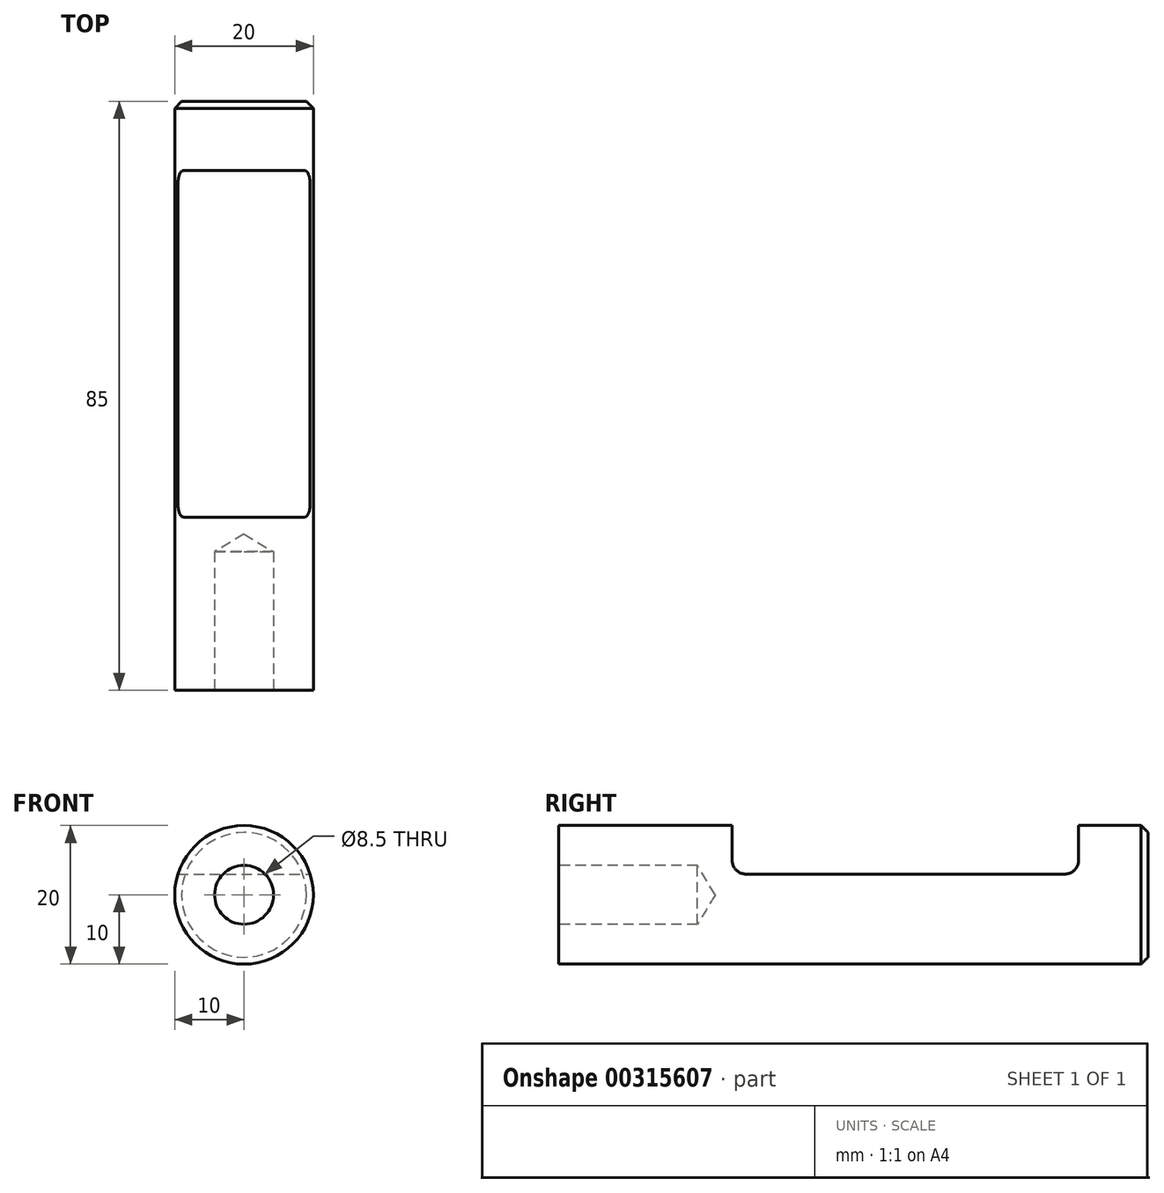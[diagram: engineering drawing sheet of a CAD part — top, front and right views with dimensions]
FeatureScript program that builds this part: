
annotation { "Feature Type Name" : "Feature", "Feature Type Description" : "" }
export const myFeature = defineFeature(function(context is Context, id is Id, definition is map)
    precondition{}
    {
        {
            var Q0;
            Q0=qCreatedBy(makeId("Front.planeOp"),FACE);
            var sketch = newSketch(context, id + "F0", { "sketchPlane" : qUnion([Q0])});
            skCircle(sketch, "E0", {"center": v(0, 0) * mm, "radius": 10 * mm});
            skSolve(sketch);
        }
        {
            var Q0;
            Q0 = qSketchRegion(id + "F0", true);
            extrude(context, id + "F1", {"entities" : qUnion([Q0]), "endBound" : BoundingType.SYMMETRIC, "depth" : 85 * mm});
        }
        {
            var Q0;
            Q0=makeQuery(id+"F1.opExtrude","CAP_FACE",FACE,{"disambiguationData":[OSD([sQuery(id+"F0.wireOp",EDGE,"E0")])],"isStart":false});
            var sketch = newSketch(context, id + "F2", { "sketchPlane" : qUnion([Q0])});
            skCircle(sketch, "E1", {"center": v(0, 0) * mm, "radius": 4.25 * mm});
            skSolve(sketch);
        }
        {
            var Q0;
            Q0=sQuery(id+"F2.wireOp",VERTEX,"E1.center");
            var Q1;
            Q1=makeQuery(id+"F1.opExtrude","SWEPT_BODY",BODY,{"disambiguationData":[OSD([sQuery(id+"F0.wireOp",EDGE,"E0")])]});
            hole(context, id + "F3", {"style" : HoleStyle.SIMPLE, "endStyle" : HoleEndStyle.BLIND, "holeDiameter" : 8.5 * mm, "holeDepth" : 20 * mm, "tappedDepth" : 12 * mm, "tapClearance" : 3, "locations" : qUnion([Q0]), "scope" : qUnion([Q1])});
        }
        {
            var Q0;
            Q0=makeQuery(id+"F1.opExtrude","CAP_EDGE",EDGE,{"disambiguationData":[OSD([sQuery(id+"F0.wireOp",EDGE,"E0")])],"isStart":true});
            chamfer(context, id + "F4", {"entities" : qUnion([Q0]), "width" : 1 * mm, "tangentPropagation" : true});
        }
        {
            var Q0;
            Q0=qCreatedBy(makeId("Right.planeOp"),FACE);
            var sketch = newSketch(context, id + "F5", { "sketchPlane" : qUnion([Q0])});
            skLineSegment(sketch, "E2.bottom", {"start": v(-17.5, 10) * mm, "end": v(32.5, 10) * mm});
            skLineSegment(sketch, "E2.top", {"start": v(-17.5, 3) * mm, "end": v(32.5, 3) * mm});
            skLineSegment(sketch, "E2.left", {"start": v(-17.5, 10) * mm, "end": v(-17.5, 3) * mm});
            skLineSegment(sketch, "E2.right", {"start": v(32.5, 10) * mm, "end": v(32.5, 3) * mm});
            skSolve(sketch);
        }
        {
            var Q0;
            Q0 = qSketchRegion(id + "F5", true);
            extrude(context, id + "F6", {"entities" : qUnion([Q0]), "operationType" : NewBodyOperationType.REMOVE, "endBound" : BoundingType.THROUGH_ALL, "oppositeDirection" : true, "depth" : 25 * mm, "hasSecondDirection" : true, "secondDirectionBound" : SecondDirectionBoundingType.THROUGH_ALL, "secondDirectionOppositeDirection" : false, "secondDirectionDepth" : 25 * mm});
        }
        {
            var Q0;
            Q0=makeQuery(id+"F6.boolean.opBoolean","COPY",EDGE,{"derivedFrom":makeQuery(id+"F6.opExtrude","SWEPT_EDGE",EDGE,{"disambiguationData":[OSD([sQuery(id+"F5.wireOp",EDGE,"E2.top"),sQuery(id+"F5.wireOp",EDGE,"E2.left")])]})});
            var Q1;
            Q1=makeQuery(id+"F6.boolean.opBoolean","COPY",EDGE,{"derivedFrom":makeQuery(id+"F6.opExtrude","SWEPT_EDGE",EDGE,{"disambiguationData":[OSD([sQuery(id+"F5.wireOp",EDGE,"E2.top"),sQuery(id+"F5.wireOp",EDGE,"E2.right")])]})});
            fillet(context, id + "F7", {"entities" : qUnion([Q0, Q1]), "radius" : 2 * mm, "tangentPropagation" : true, "allowEdgeOverflow" : false});
        }
    });
